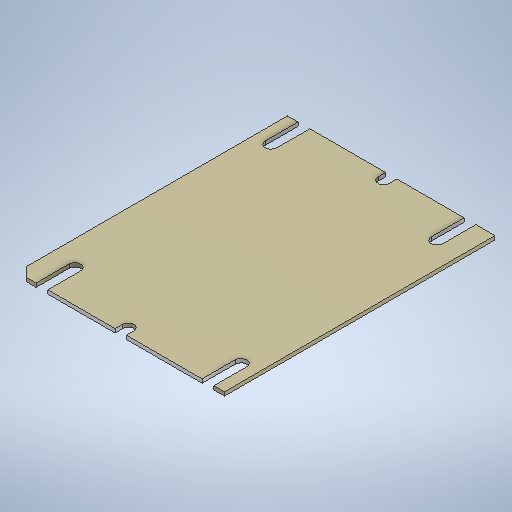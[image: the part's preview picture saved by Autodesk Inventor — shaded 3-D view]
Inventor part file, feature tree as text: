
AUTODESK INVENTOR PART (.ipt)
format: ipt  version: 2025 (Build 290162000, 162)  size: 348,160 bytes
history: native  units: in
note: dims shown in document units (in); Inventor stores cm internally (conversion verified against a paired STEP export)
features: extrude x4, sketch x2, hole x1
ambient origin geometry x8: Origin, YZ Plane, XZ Plane, XY Plane, X Axis, Y Axis, Z Axis, Center Point
bodies: Body1 (feature_tree)
feature tree (7):
  extrude  "Extrusion2"  Depth=2.2638in
  extrude  "Extrusion3"  Depth=0.0984in
  hole  "Hole1"  [1 undecoded]
  extrude  "Extrusion4"  Depth=0.0492in
  extrude  "Extrusion5"  TaperAngle=0.0deg  [1 undecoded]
  sketch  "Sketch3"  dims[d28=1.7362in d29=2.2638in]
  sketch  "Sketch6"  dims[d30=0.0315in d31=0.0in d32=0.0984in d33=0.2756in d34=0.0492in d35=0.0in d36=0.0in d37=0.8681in d38=0.063in d40=0.063in d41=0.0945in d42=0.1575in d43=0.1732in d44=0.0787in d45=0.6181in d46=0.315in d47=0.8108in d48=0.2087in d49=0.0787in d50=0.0787in d51=0.0in d52=0.0in d60=0.2756in d61=0.2756in d62=0.0492in d64=0.2756in d65=0.2756in d66=0.0492in d68=1.7362in d69=0.3937in d70=0.0in d71=0.1378in d87=0.2087in d88=0.1378in]
note: 2 required parameter values undecoded (feature->parameter linkage not recoverable at this tier; creation-order binding heuristic only, values carry confidence <= 0.55)
